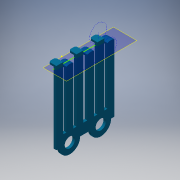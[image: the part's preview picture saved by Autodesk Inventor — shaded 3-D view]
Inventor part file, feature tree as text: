
AUTODESK INVENTOR PART (.ipt)
format: ipt  version: 2016 (Build 200138000, 138)  size: 410,112 bytes
history: native  units: in
note: dims shown in document units (in); Inventor stores cm internally (conversion verified against a paired STEP export)
features: sketch x14, extrude x13, projected_geometry x9, reference x8, plane x6, fillet x2, mirror x1, imported_body x1, boolean_combine x1
ambient origin geometry x8: Origin, YZ Plane, XZ Plane, XY Plane, X Axis, Y Axis, Z Axis, Center Point
bodies: Solid1 (feature_tree), Solid2 (feature_tree)
feature tree (55):
  extrude  "Extrusion1"  Depth=0.0079in
  sketch  "Sketch2"  dims[d11=0.0079in d12=0.052in d13=0.052in]
  plane  "Work Plane1"
  plane  "Work Plane2"
  extrude  "Extrusion2"  Depth=0.052in
  fillet  "Fillet1"  Radius=0.052in
  extrude  "Extrusion3"  Depth=0.052in
  sketch  "Sketch4"  dims[d16=0.025in d17=0.025in d18=0.0197in d19=0.0in]
  plane  "Work Plane3"
  extrude  "Extrusion5"  Depth=0.025in
  fillet  "Fillet3"  Radius=0.0197in
  sketch  "Sketch6"  dims[d23=0.3937in d24=0.0in d25=0.0787in]
  plane  "Work Plane4"
  mirror  "Mirror1"
  extrude  "Extrusion6"  Depth=0.0197in
  plane  "Work Plane5"
  extrude  "Extrusion7"  Depth=0.0787in
  extrude  "Extrusion8"  Depth=0.0394in
  extrude  "Extrusion9"  Depth=0.0394in TaperAngle=0.0deg
  extrude  "Extrusion10"  TaperAngle=90.0deg  [1 undecoded]
  extrude  "Extrusion11"  Depth=0.0394in TaperAngle=0.0deg
  extrude  "Extrusion12"  Depth=0.0492in TaperAngle=0.0deg
  extrude  "Extrusion13"  Depth=0.0394in TaperAngle=0.0deg
  imported_body  "Base1"
  boolean_combine  "Combine1"
  sketch  "Sketch14"  dims[d55=1.0in d56=0.0in]
  plane  "Work Plane6"
  extrude  "Extrusion14"  Depth=0.0157in TaperAngle=0.0deg
  sketch  "Sketch1"  dims[d9=0.0079in d10=0.0079in]
  reference  "Reference1"
  reference  "Reference2"
  reference  "Reference3"
  reference  "Reference4"
  reference  "Reference5"
  sketch  "Sketch3"  dims[d14=0.052in d15=0.0079in]
  projected_geometry  "Projected Loop1"
  projected_geometry  "Projected Loop2"
  projected_geometry  "Projected Loop3"
  projected_geometry  "Projected Loop4"
  projected_geometry  "Projected Loop5"
  projected_geometry  "Projected Loop6"
  sketch  "Sketch5"  dims[d20=0.0197in d21=0.0in d22=0.0197in]
  reference  "Reference6"
  reference  "Reference7"
  reference  "Reference8"
  sketch  "Sketch7"  dims[d29=0.0394in d30=0.0394in]
  sketch  "Sketch8"  dims[d31=0.1181in d32=0.0394in d33=0.0in]
  sketch  "Sketch9"  dims[d34=0.0157in d36=90.0deg]
  projected_geometry  "Projected Loop7"
  projected_geometry  "Projected Loop8"
  sketch  "Sketch10"  dims[d37=0.0394in d38=0.0in d39=0.0492in d40=0.0in]
  sketch  "Sketch11"  dims[d41=0.0in d42=0.0in d43=0.0492in d44=0.0in]
  sketch  "Sketch12"  dims[d45=0.0394in d46=0.0in d48=0.0394in d49=0.0in]
  sketch  "Sketch13"  dims[d50=0.0394in d51=0.0in d52=0.0157in d53=0.0in]
  projected_geometry  "Projected Loop9"
note: 1 required parameter value undecoded (feature->parameter linkage not recoverable at this tier; creation-order binding heuristic only, values carry confidence <= 0.55)
